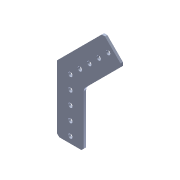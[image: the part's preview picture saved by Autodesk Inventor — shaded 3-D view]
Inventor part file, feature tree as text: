
AUTODESK INVENTOR PART (.ipt)
format: ipt  version: 2013 (Build 170138000, 138)  size: 103,424 bytes
history: native  units: in
note: dims shown in document units (in); Inventor stores cm internally (conversion verified against a paired STEP export)
features: fillet x1, other x1, imported_body x1
ambient origin geometry x8: Origin, YZ Plane, XZ Plane, XY Plane, X Axis, Y Axis, Z Axis, Center Point
feature tree (3):
  fillet  "Fillet2"  [1 undecoded]
  other  "217-3556-STEP1"
  imported_body  "Base1"
note: 1 required parameter value undecoded (feature->parameter linkage not recoverable at this tier; creation-order binding heuristic only, values carry confidence <= 0.55)
